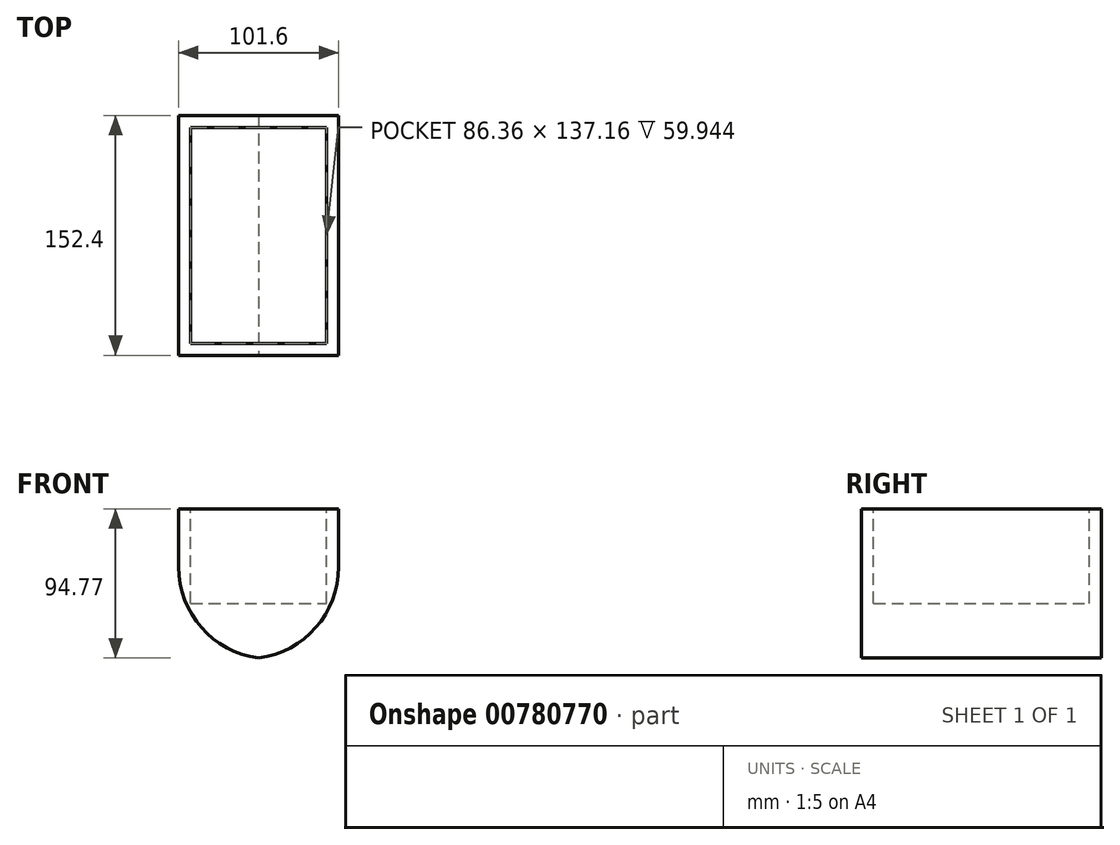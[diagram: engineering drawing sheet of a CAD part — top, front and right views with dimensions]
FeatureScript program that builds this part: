
annotation { "Feature Type Name" : "Feature", "Feature Type Description" : "" }
export const myFeature = defineFeature(function(context is Context, id is Id, definition is map)
    precondition{}
    {
        {
            var Q0;
            Q0=qCreatedBy(makeId("Top.planeOp"),FACE);
            var sketch = newSketch(context, id + "F0", { "sketchPlane" : qUnion([Q0])});
            skLineSegment(sketch, "E0.bottom", {"start": v(-48.53, -72.48) * mm, "end": v(53.07, -72.48) * mm});
            skLineSegment(sketch, "E0.top", {"start": v(-48.53, 79.92) * mm, "end": v(53.07, 79.92) * mm});
            skLineSegment(sketch, "E0.left", {"start": v(-48.53, -72.48) * mm, "end": v(-48.53, 79.92) * mm});
            skLineSegment(sketch, "E0.right", {"start": v(53.07, -72.48) * mm, "end": v(53.07, 79.92) * mm});
            skSolve(sketch);
        }
        {
            var Q0;
            Q0=makeQuery(id+"F0.imprint","IMPRINT",FACE,{"disambiguationData":[TD([[makeQuery(id+"F0.imprint","IMPRINT",EDGE,{"derivedFrom":sQuery(id+"F0.wireOp",EDGE,"E0.bottom")}),1.0]])]});
            extrude(context, id + "F1", {"entities" : qUnion([Q0]), "depth" : 95.25 * mm, "offsetDistance" : 25.4 * mm});
        }
        {
            var Q0;
            Q0=makeQuery(id+"F1.opExtrude","CAP_EDGE",EDGE,{"disambiguationData":[OSD([sQuery(id+"F0.wireOp",EDGE,"E0.left")])],"isStart":true});
            var Q1;
            Q1=makeQuery(id+"F1.opExtrude","CAP_EDGE",EDGE,{"disambiguationData":[OSD([sQuery(id+"F0.wireOp",EDGE,"E0.right")])],"isStart":true});
            fillet(context, id + "F2", {"entities" : qUnion([Q0, Q1]), "radius" : 58.25 * mm, "tangentPropagation" : true, "allowEdgeOverflow" : false});
        }
        {
            var Q0;
            Q0=makeQuery(id+"F1.opExtrude","CAP_FACE",FACE,{"disambiguationData":[OSD([sQuery(id+"F0.wireOp",EDGE,"E0.bottom"),sQuery(id+"F0.wireOp",EDGE,"E0.top"),sQuery(id+"F0.wireOp",EDGE,"E0.left"),sQuery(id+"F0.wireOp",EDGE,"E0.right")])],"isStart":false});
            var sketch = newSketch(context, id + "F3", { "sketchPlane" : qUnion([Q0])});
            skLineSegment(sketch, "E1.bottom", {"start": v(-40.9, -64.86) * mm, "end": v(45.45, -64.86) * mm});
            skLineSegment(sketch, "E1.top", {"start": v(-40.9, 72.3) * mm, "end": v(45.45, 72.3) * mm});
            skLineSegment(sketch, "E1.left", {"start": v(-40.9, -64.86) * mm, "end": v(-40.9, 72.3) * mm});
            skLineSegment(sketch, "E1.right", {"start": v(45.45, -64.86) * mm, "end": v(45.45, 72.3) * mm});
            skLineSegment(sketch, "E2", {"start": v(-48.53, 17.4) * mm, "end": v(-40.9, 17.4) * mm});
            skLineSegment(sketch, "E3", {"start": v(45.45, 17.99) * mm, "end": v(53.07, 17.99) * mm});
            skSolve(sketch);
        }
        {
            var Q0;
            Q0 = qSketchRegion(id + "F3", true);
            extrude(context, id + "F4", {"entities" : qUnion([Q0]), "operationType" : NewBodyOperationType.REMOVE, "oppositeDirection" : true, "depth" : 59.94 * mm, "offsetDistance" : 25.4 * mm});
        }
    });
